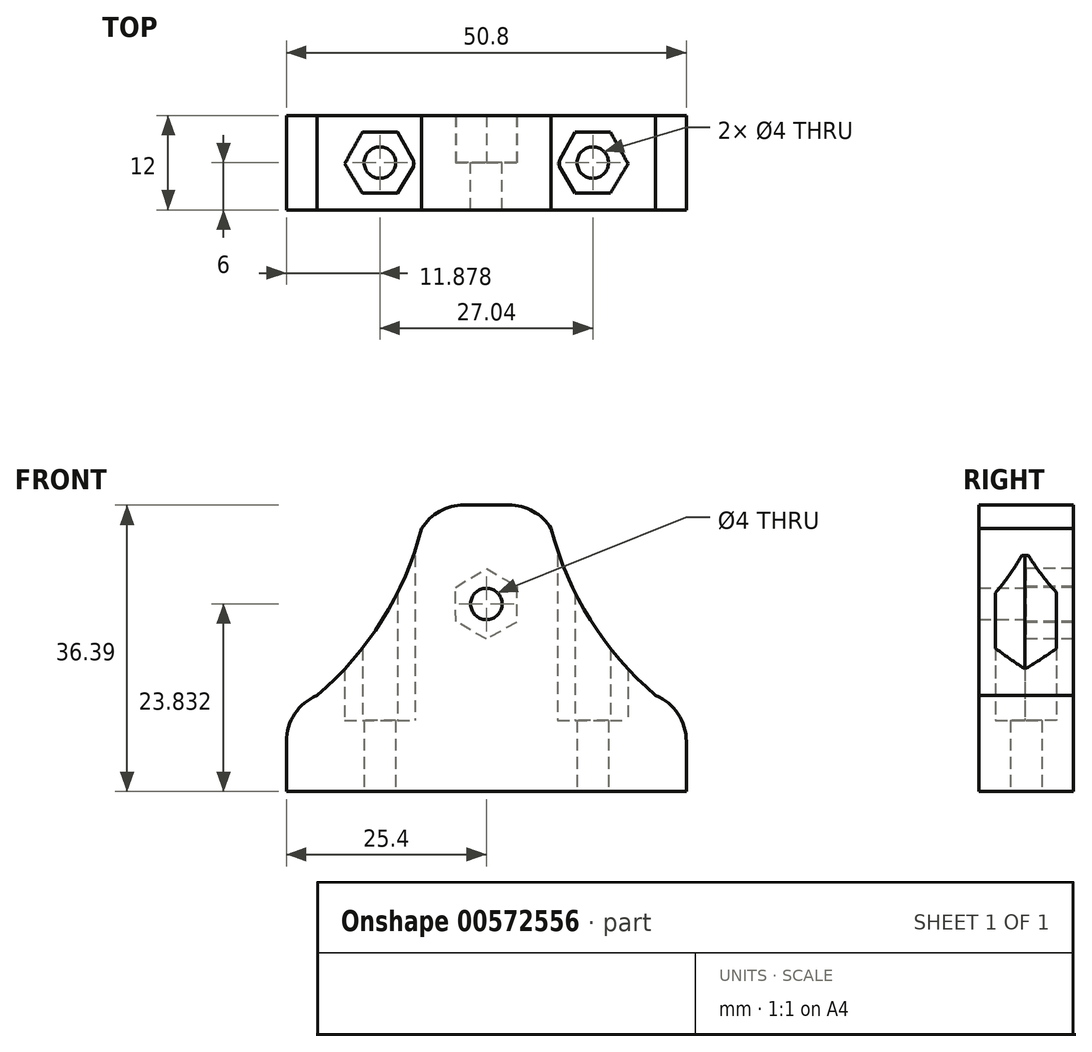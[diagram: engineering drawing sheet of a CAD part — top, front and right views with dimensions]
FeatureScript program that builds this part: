
annotation { "Feature Type Name" : "Feature", "Feature Type Description" : "" }
export const myFeature = defineFeature(function(context is Context, id is Id, definition is map)
    precondition{}
    {
        {
            var Q0;
            Q0=qCreatedBy(makeId("Top.planeOp"),FACE);
            var sketch = newSketch(context, id + "F0", { "sketchPlane" : qUnion([Q0])});
            skLineSegment(sketch, "E0.bottom", {"start": v(-16.1, 4.45) * mm, "end": v(3.9, 4.45) * mm});
            skLineSegment(sketch, "E0.top", {"start": v(-16.1, -5.55) * mm, "end": v(3.9, -5.55) * mm});
            skLineSegment(sketch, "E0.left", {"start": v(-16.1, 4.45) * mm, "end": v(-16.1, -5.55) * mm});
            skLineSegment(sketch, "E0.right", {"start": v(3.9, 4.45) * mm, "end": v(3.9, -5.55) * mm});
            skLineSegment(sketch, "E1.bottom", {"start": v(-16.1, 1.45) * mm, "end": v(3.9, 1.45) * mm});
            skLineSegment(sketch, "E1.top", {"start": v(-16.1, -3.55) * mm, "end": v(3.9, -3.55) * mm});
            skLineSegment(sketch, "E1.left", {"start": v(-16.1, 1.45) * mm, "end": v(-16.1, -3.55) * mm});
            skLineSegment(sketch, "E1.right", {"start": v(3.9, 1.45) * mm, "end": v(3.9, -3.55) * mm});
            skSolve(sketch);
        }
        {
            var Q0;
            Q0=makeQuery(id+"F0.imprint","IMPRINT",FACE,{"disambiguationData":[TD([[makeQuery(id+"F0.imprint","IMPRINT",EDGE,{"derivedFrom":sQuery(id+"F0.wireOp",EDGE,"E1.bottom")}),-1.0]])]});
            extrude(context, id + "F1", {"entities" : qUnion([Q0]), "depth" : 3 * mm, "offsetDistance" : 25.4 * mm});
        }
        {
            var Q0;
            {var subQ0=sQuery(id+"F0.wireOp",EDGE,"E0.bottom");Q0=makeQuery(id+"F0.imprint","IMPRINT",FACE,{"disambiguationData":[TD([[makeQuery(id+"F0.imprint","IMPRINT",EDGE,{"derivedFrom":subQ0}),-1.0]])]});}
            var Q1;
            {var subQ0=sQuery(id+"F0.wireOp",EDGE,"E0.top");Q1=makeQuery(id+"F0.imprint","IMPRINT",FACE,{"disambiguationData":[TD([[makeQuery(id+"F0.imprint","IMPRINT",EDGE,{"derivedFrom":subQ0}),1.0]])]});}
            extrude(context, id + "F2", {"entities" : qUnion([Q0, Q1]), "operationType" : NewBodyOperationType.ADD, "depth" : 15 * mm, "offsetDistance" : 25.4 * mm});
        }
        {
            var Q0;
            Q0=makeQuery(id+"F2.opExtrude","SWEPT_FACE",FACE,{"disambiguationData":[OSD([sQuery(id+"F0.wireOp",EDGE,"E0.bottom")])]});
            var sketch = newSketch(context, id + "F3", { "sketchPlane" : qUnion([Q0])});
            skLineSegment(sketch, "E2.0", {"start": v(8.35, 13) * mm, "end": v(10.58, 8.99) * mm});
            skLineSegment(sketch, "E2.1", {"start": v(10.58, 8.99) * mm, "end": v(8.35, 5.25) * mm});
            skLineSegment(sketch, "E2.2", {"start": v(8.35, 5.25) * mm, "end": v(3.87, 5.25) * mm});
            skLineSegment(sketch, "E2.3", {"start": v(3.87, 5.25) * mm, "end": v(1.63, 8.99) * mm});
            skLineSegment(sketch, "E2.4", {"start": v(1.63, 8.99) * mm, "end": v(3.87, 13) * mm});
            skLineSegment(sketch, "E2.5", {"start": v(3.87, 13) * mm, "end": v(8.35, 13) * mm});
            skCircle(sketch, "E3", {"center": v(6.1, 9.12) * mm, "radius": 2 * mm});
            skSolve(sketch);
        }
        {
            var Q0;
            Q0=makeQuery(id+"F3.imprint","IMPRINT",FACE,{"disambiguationData":[TD([[makeQuery(id+"F3.imprint","IMPRINT",EDGE,{"derivedFrom":sQuery(id+"F3.wireOp",EDGE,"E2.0")}),-1.0]])]});
            extrude(context, id + "F4", {"entities" : qUnion([Q0]), "operationType" : NewBodyOperationType.REMOVE, "oppositeDirection" : true, "depth" : 2 * mm, "offsetDistance" : 25.4 * mm});
        }
        {
            var Q0;
            Q0=makeQuery(id+"F4.boolean.opBoolean","SPLIT",FACE,{"disambiguationData":[TD([makeQuery(id+"F4.opExtrude","SWEPT_FACE",FACE,{"disambiguationData":[OSD([sQuery(id+"F3.wireOp",EDGE,"E3")])]})])],"derivedFrom":makeQuery(id+"F2.opExtrude","SWEPT_FACE",FACE,{"disambiguationData":[OSD([sQuery(id+"F0.wireOp",EDGE,"E0.bottom")])]})});
            extrude(context, id + "F5", {"entities" : qUnion([Q0]), "operationType" : NewBodyOperationType.REMOVE, "oppositeDirection" : true, "depth" : 25.4 * mm, "offsetDistance" : 25.4 * mm});
        }
        {
            var Q0;
            Q0=qCreatedBy(makeId("Front.planeOp"),FACE);
            var sketch = newSketch(context, id + "F6", { "sketchPlane" : qUnion([Q0])});
            skLineSegment(sketch, "E4", {"start": v(-25.4, 0) * mm, "end": v(25.4, 0) * mm});
            skLineSegment(sketch, "E5", {"start": v(25.4, 0) * mm, "end": v(25.4, 6.35) * mm});
            skLineSegment(sketch, "E6", {"start": v(-25.4, 6.35) * mm, "end": v(-25.4, 0) * mm});
            skLineSegment(sketch, "E7.0", {"start": v(3.87, 26.07) * mm, "end": v(3.8, 21.47) * mm});
            skLineSegment(sketch, "E7.1", {"start": v(3.8, 21.47) * mm, "end": v(0, 19.36) * mm});
            skLineSegment(sketch, "E7.2", {"start": v(0, 19.36) * mm, "end": v(-3.88, 21.6) * mm});
            skLineSegment(sketch, "E7.3", {"start": v(-3.88, 21.6) * mm, "end": v(-3.94, 25.95) * mm});
            skLineSegment(sketch, "E7.4", {"start": v(-3.94, 25.95) * mm, "end": v(0, 28.3) * mm});
            skLineSegment(sketch, "E7.5", {"start": v(0, 28.3) * mm, "end": v(3.88, 26.07) * mm});
            skCircle(sketch, "E8", {"center": v(0, 23.83) * mm, "radius": 2 * mm});
            skPoint(sketch, "E9.visualSharp", {"position": v(-25.4, 10.94) * mm});
            skArc(sketch, "E9.filletArc", {"start": v(-21.5, 12.2) * mm, "mid": v(-24.34, 9.87) * mm, "end": v(-25.4, 6.35) * mm});
            skPoint(sketch, "E10.visualSharp", {"position": v(25.4, 10.94) * mm});
            skArc(sketch, "E10.filletArc", {"start": v(25.4, 6.35) * mm, "mid": v(24.34, 9.87) * mm, "end": v(21.5, 12.2) * mm});
            skLineSegment(sketch, "E11", {"start": v(-2.85, 36.39) * mm, "end": v(2.85, 36.39) * mm});
            skPoint(sketch, "E12.visualSharp", {"position": v(-6.37, 36.39) * mm});
            skArc(sketch, "E12.filletArc", {"start": v(-2.85, 36.39) * mm, "mid": v(-5.93, 35.6) * mm, "end": v(-8.23, 33.4) * mm});
            skPoint(sketch, "E13.visualSharp", {"position": v(6.37, 36.39) * mm});
            skArc(sketch, "E13.filletArc", {"start": v(8.23, 33.4) * mm, "mid": v(5.93, 35.6) * mm, "end": v(2.85, 36.39) * mm});
            skArc(sketch, "E14", {"start": v(-21.5, 12.2) * mm, "mid": v(-13.23, 21.78) * mm, "end": v(-8.23, 33.4) * mm});
            skArc(sketch, "E15", {"start": v(8.23, 33.4) * mm, "mid": v(13.23, 21.78) * mm, "end": v(21.5, 12.2) * mm});
            skSolve(sketch);
        }
        {
            var Q0;
            Q0=makeQuery(id+"F6.imprint","IMPRINT",FACE,{"disambiguationData":[TD([[makeQuery(id+"F6.imprint","IMPRINT",EDGE,{"derivedFrom":sQuery(id+"F6.wireOp",EDGE,"E4")}),1.0]])]});
            var Q1;
            Q1=makeQuery(id+"F6.imprint","IMPRINT",FACE,{"disambiguationData":[TD([[makeQuery(id+"F6.imprint","IMPRINT",EDGE,{"derivedFrom":sQuery(id+"F6.wireOp",EDGE,"E7.0")}),-1.0]])]});
            extrude(context, id + "F7", {"entities" : qUnion([Q0, Q1]), "depth" : 6 * mm, "offsetDistance" : 25.4 * mm});
        }
        {
            var Q0;
            Q0=makeQuery(id+"F6.imprint","IMPRINT",FACE,{"disambiguationData":[TD([[makeQuery(id+"F6.imprint","IMPRINT",EDGE,{"derivedFrom":sQuery(id+"F6.wireOp",EDGE,"E4")}),1.0]])]});
            extrude(context, id + "F8", {"entities" : qUnion([Q0]), "operationType" : NewBodyOperationType.ADD, "oppositeDirection" : true, "depth" : 6 * mm, "offsetDistance" : 25.4 * mm});
        }
        {
            var Q0;
            Q0=qCreatedBy(makeId("Top.planeOp"),FACE);
            var sketch = newSketch(context, id + "F9", { "sketchPlane" : qUnion([Q0])});
            skLineSegment(sketch, "E16.0.0", {"start": v(-6.37, -6) * mm, "end": v(-6.37, 6) * mm});
            skLineSegment(sketch, "E16.0.1", {"start": v(-6.37, 6) * mm, "end": v(-20.67, 6) * mm});
            skLineSegment(sketch, "E16.0.2", {"start": v(-20.67, 6) * mm, "end": v(-20.67, -6) * mm});
            skLineSegment(sketch, "E16.0.3", {"start": v(-20.67, -6) * mm, "end": v(-6.37, -6) * mm});
            skLineSegment(sketch, "E16.1.0", {"start": v(20.67, -6) * mm, "end": v(20.67, 6) * mm});
            skLineSegment(sketch, "E16.1.1", {"start": v(20.67, 6) * mm, "end": v(6.37, 6) * mm});
            skLineSegment(sketch, "E16.1.2", {"start": v(6.37, 6) * mm, "end": v(6.37, -6) * mm});
            skLineSegment(sketch, "E16.1.3", {"start": v(6.37, -6) * mm, "end": v(20.67, -6) * mm});
            skLineSegment(sketch, "E17.0", {"start": v(-11.28, 3.87) * mm, "end": v(-9.05, -0.14) * mm});
            skLineSegment(sketch, "E17.1", {"start": v(-9.05, -0.14) * mm, "end": v(-11.28, -3.88) * mm});
            skLineSegment(sketch, "E17.2", {"start": v(-11.28, -3.88) * mm, "end": v(-15.76, -3.88) * mm});
            skLineSegment(sketch, "E17.3", {"start": v(-15.76, -3.88) * mm, "end": v(-18, -0.14) * mm});
            skLineSegment(sketch, "E17.4", {"start": v(-18, -0.14) * mm, "end": v(-15.76, 3.88) * mm});
            skLineSegment(sketch, "E17.5", {"start": v(-15.76, 3.87) * mm, "end": v(-11.28, 3.87) * mm});
            skCircle(sketch, "E18", {"center": v(-13.52, 0) * mm, "radius": 2 * mm});
            skLineSegment(sketch, "E19.0", {"start": v(15.76, 3.87) * mm, "end": v(18, -0.14) * mm});
            skLineSegment(sketch, "E19.1", {"start": v(18, -0.14) * mm, "end": v(15.76, -3.88) * mm});
            skLineSegment(sketch, "E19.2", {"start": v(15.76, -3.88) * mm, "end": v(11.28, -3.87) * mm});
            skLineSegment(sketch, "E19.3", {"start": v(11.28, -3.87) * mm, "end": v(9.04, -0.14) * mm});
            skLineSegment(sketch, "E19.4", {"start": v(9.04, -0.14) * mm, "end": v(11.28, 3.88) * mm});
            skLineSegment(sketch, "E19.5", {"start": v(11.28, 3.88) * mm, "end": v(15.76, 3.87) * mm});
            skCircle(sketch, "E20", {"center": v(13.52, 0) * mm, "radius": 2 * mm});
            skSolve(sketch);
        }
        {
            var Q0;
            Q0=makeQuery(id+"F9.imprint","IMPRINT",FACE,{"disambiguationData":[TD([[makeQuery(id+"F9.imprint","IMPRINT",EDGE,{"derivedFrom":sQuery(id+"F9.wireOp",EDGE,"E18")}),1.0]])]});
            var Q1;
            Q1=makeQuery(id+"F9.imprint","IMPRINT",FACE,{"disambiguationData":[TD([[makeQuery(id+"F9.imprint","IMPRINT",EDGE,{"derivedFrom":sQuery(id+"F9.wireOp",EDGE,"E20")}),1.0]])]});
            extrude(context, id + "F10", {"entities" : qUnion([Q0, Q1]), "operationType" : NewBodyOperationType.REMOVE, "depth" : 25.4 * mm, "offsetDistance" : 25.4 * mm});
        }
        {
            var Q0;
            Q0=makeQuery(id+"F9.imprint","IMPRINT",FACE,{"disambiguationData":[TD([[makeQuery(id+"F9.imprint","IMPRINT",EDGE,{"derivedFrom":sQuery(id+"F9.wireOp",EDGE,"E17.0")}),-1.0]])]});
            var Q1;
            Q1=makeQuery(id+"F9.imprint","IMPRINT",FACE,{"disambiguationData":[TD([[makeQuery(id+"F9.imprint","IMPRINT",EDGE,{"derivedFrom":sQuery(id+"F9.wireOp",EDGE,"E19.0")}),-1.0]])]});
            extrude(context, id + "F11", {"entities" : qUnion([Q0, Q1]), "operationType" : NewBodyOperationType.REMOVE, "depth" : 30 * mm, "offsetDistance" : 25.4 * mm, "hasSecondDirection" : true, "secondDirectionOppositeDirection" : false, "secondDirectionDepth" : 9 * mm});
        }
    });
